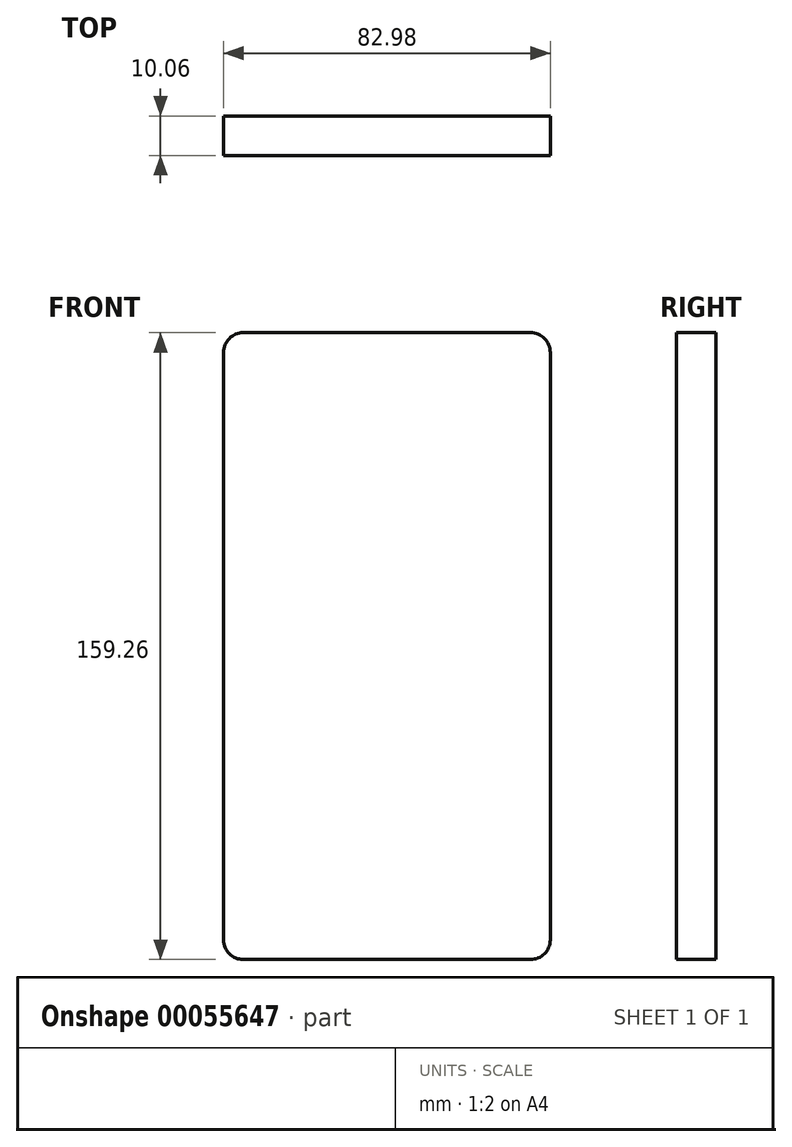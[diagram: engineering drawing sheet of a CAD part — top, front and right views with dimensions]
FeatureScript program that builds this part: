
annotation { "Feature Type Name" : "Feature", "Feature Type Description" : "" }
export const myFeature = defineFeature(function(context is Context, id is Id, definition is map)
    precondition{}
    {
        {
            assignVariable(context, id + "F0", {"name" : "PhoneDepth", "anyValue" : 10.06 * mm});
        }
        {
            var Q0;
            Q0=qCreatedBy(makeId("Front.planeOp"),FACE);
            var sketch = newSketch(context, id + "F1", { "sketchPlane" : qUnion([Q0])});
            skLineSegment(sketch, "E0.bottom", {"start": v(-3.42, 96.42) * mm, "end": v(69.56, 96.42) * mm});
            skLineSegment(sketch, "E0.top", {"start": v(-3.42, -62.84) * mm, "end": v(69.56, -62.84) * mm});
            skLineSegment(sketch, "E0.left", {"start": v(-8.42, 91.42) * mm, "end": v(-8.42, -57.84) * mm});
            skLineSegment(sketch, "E0.right", {"start": v(74.56, 91.42) * mm, "end": v(74.56, -57.84) * mm});
            skPoint(sketch, "E1.visualSharp", {"position": v(-8.42, 96.42) * mm});
            skArc(sketch, "E1.filletArc", {"start": v(-3.42, 96.42) * mm, "mid": v(-6.96, 94.96) * mm, "end": v(-8.42, 91.42) * mm});
            skPoint(sketch, "E2.visualSharp", {"position": v(-8.42, -62.84) * mm});
            skArc(sketch, "E2.filletArc", {"start": v(-8.42, -57.84) * mm, "mid": v(-6.96, -61.37) * mm, "end": v(-3.42, -62.84) * mm});
            skPoint(sketch, "E3.visualSharp", {"position": v(74.56, -62.84) * mm});
            skArc(sketch, "E3.filletArc", {"start": v(69.56, -62.84) * mm, "mid": v(73.1, -61.37) * mm, "end": v(74.56, -57.84) * mm});
            skPoint(sketch, "E4.visualSharp", {"position": v(74.56, 96.42) * mm});
            skArc(sketch, "E4.filletArc", {"start": v(74.56, 91.42) * mm, "mid": v(73.1, 94.96) * mm, "end": v(69.56, 96.42) * mm});
            skSolve(sketch);
        }
        {
            var Q0;
            Q0=makeQuery(id+"F1.imprint","IMPRINT",FACE,{"disambiguationData":[TD([[makeQuery(id+"F1.imprint","IMPRINT",EDGE,{"derivedFrom":sQuery(id+"F1.wireOp",EDGE,"E0.bottom")}),-1.0]])]});
            extrude(context, id + "F2", {"entities" : qUnion([Q0]), "depth" : getVariable(context, 'PhoneDepth')});
        }
    });
